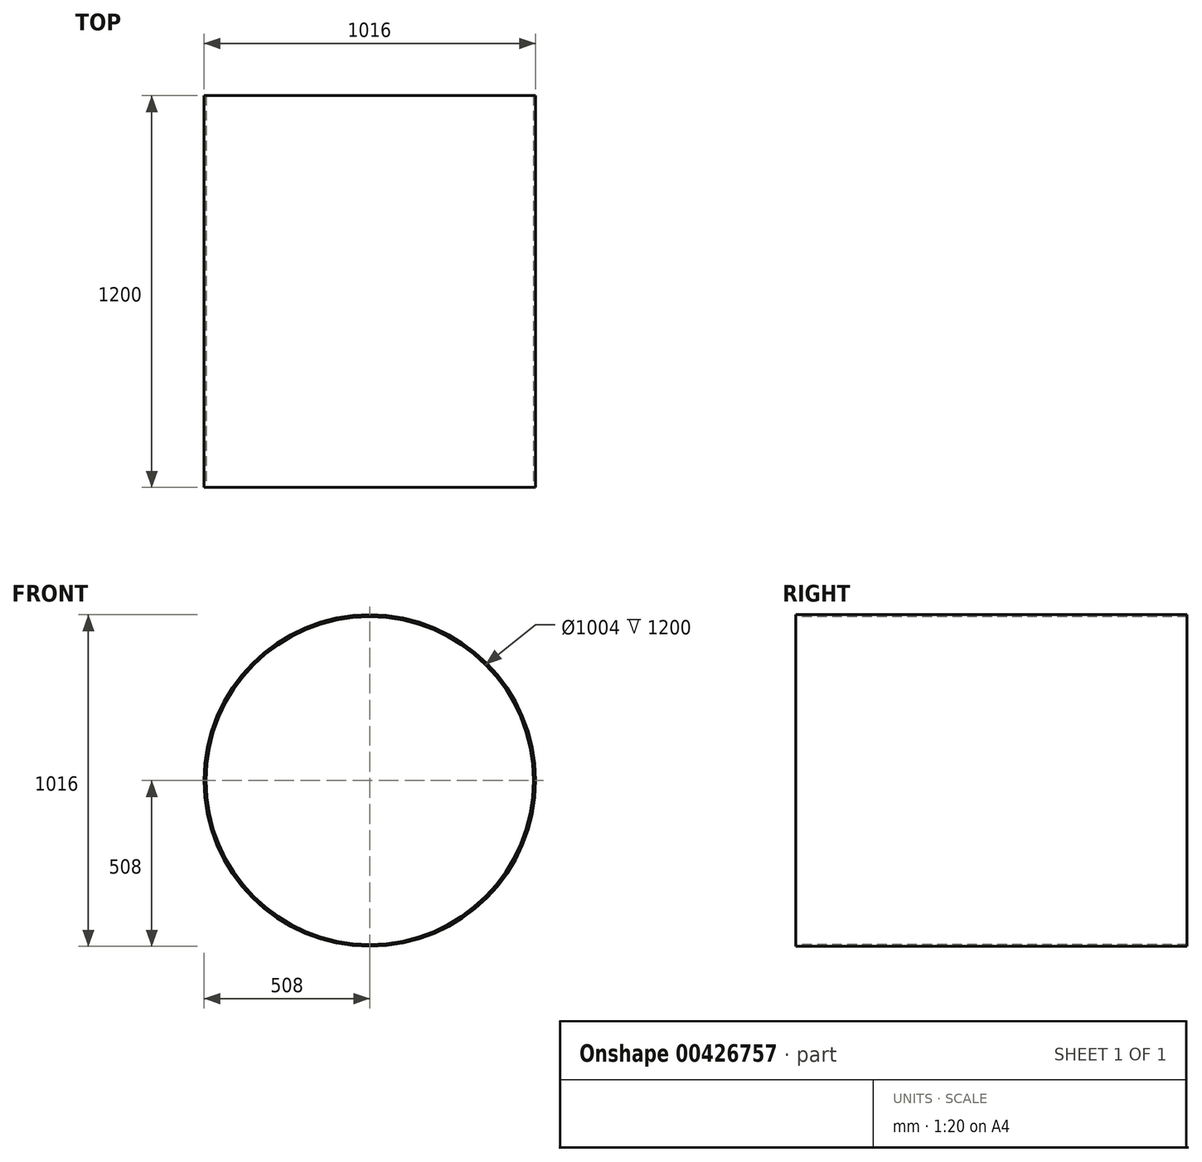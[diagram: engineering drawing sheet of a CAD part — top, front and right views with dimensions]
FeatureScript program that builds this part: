
annotation { "Feature Type Name" : "Feature", "Feature Type Description" : "" }
export const myFeature = defineFeature(function(context is Context, id is Id, definition is map)
    precondition{}
    {
        {
            var Q0;
            Q0=qCreatedBy(makeId("Front.planeOp"),FACE);
            var sketch = newSketch(context, id + "F0", { "sketchPlane" : qUnion([Q0])});
            skCircle(sketch, "E0", {"center": v(0, 0) * mm, "radius": 508 * mm});
            skCircle(sketch, "E1.0", {"center": v(0, 0) * mm, "radius": 502 * mm});
            skSolve(sketch);
        }
        {
            var Q0;
            Q0=makeQuery(id+"F0.imprint","IMPRINT",FACE,{"disambiguationData":[TD([[makeQuery(id+"F0.imprint","IMPRINT",EDGE,{"derivedFrom":sQuery(id+"F0.wireOp",EDGE,"E0")}),1.0]])]});
            extrude(context, id + "F1", {"entities" : qUnion([Q0]), "oppositeDirection" : true, "depth" : 1200 * mm});
        }
    });
